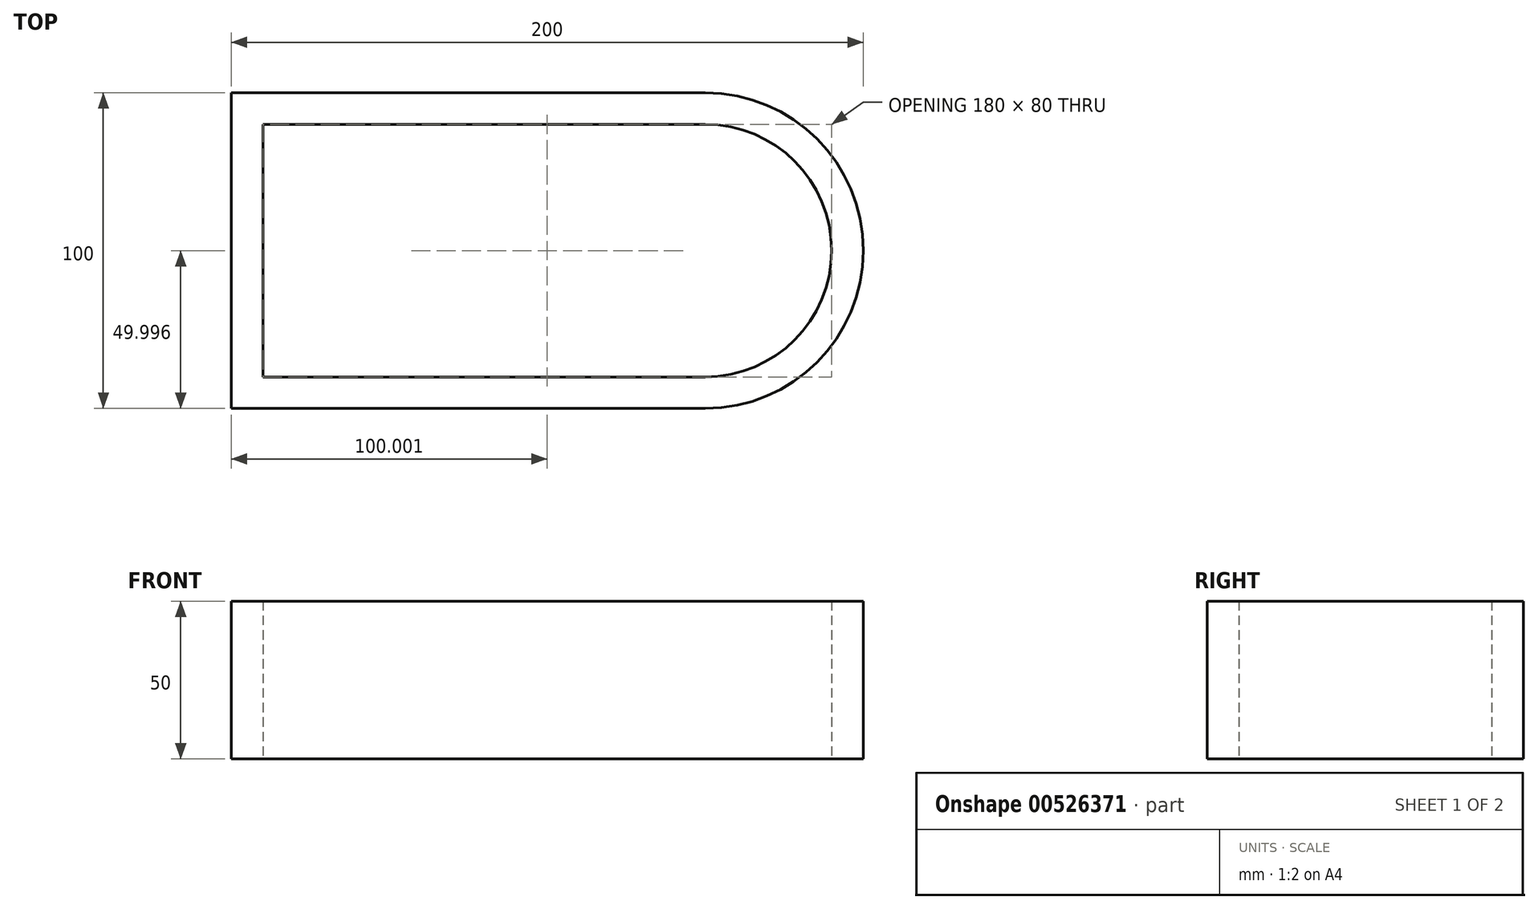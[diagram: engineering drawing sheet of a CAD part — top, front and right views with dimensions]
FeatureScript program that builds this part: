
annotation { "Feature Type Name" : "Feature", "Feature Type Description" : "" }
export const myFeature = defineFeature(function(context is Context, id is Id, definition is map)
    precondition{}
    {
        {
            var Q0;
            Q0=qCreatedBy(makeId("Top.planeOp"),FACE);
            var sketch = newSketch(context, id + "F0", { "sketchPlane" : qUnion([Q0])});
            skLineSegment(sketch, "E0.bottom", {"start": v(-110.52, 48.32) * mm, "end": v(39.48, 48.32) * mm});
            skLineSegment(sketch, "E0.top", {"start": v(-110.52, -51.68) * mm, "end": v(39.48, -51.68) * mm});
            skLineSegment(sketch, "E0.left", {"start": v(-110.52, 48.32) * mm, "end": v(-110.52, -51.68) * mm});
            skLineSegment(sketch, "E0.right", {"start": v(39.48, 48.32) * mm, "end": v(39.48, -51.68) * mm});
            skArc(sketch, "E1", {"start": v(39.48, -51.68) * mm, "mid": v(89.48, -1.68) * mm, "end": v(39.48, 48.32) * mm});
            skLineSegment(sketch, "E2.bottom", {"start": v(-100.52, 38.32) * mm, "end": v(39.48, 38.32) * mm});
            skLineSegment(sketch, "E2.top", {"start": v(-100.52, -41.68) * mm, "end": v(39.48, -41.68) * mm});
            skLineSegment(sketch, "E2.left", {"start": v(-100.52, 38.32) * mm, "end": v(-100.52, -41.68) * mm});
            skLineSegment(sketch, "E2.right", {"start": v(39.48, 38.32) * mm, "end": v(39.48, -41.68) * mm});
            skArc(sketch, "E3", {"start": v(39.48, -41.68) * mm, "mid": v(79.48, -1.68) * mm, "end": v(39.48, 38.32) * mm});
            skSolve(sketch);
        }
        {
            var Q0;
            Q0=makeQuery(id+"F0.imprint","IMPRINT",FACE,{"disambiguationData":[TD([[makeQuery(id+"F0.imprint","IMPRINT",EDGE,{"derivedFrom":sQuery(id+"F0.wireOp",EDGE,"E0.bottom")}),-1.0]])]});
            var Q1;
            Q1=makeQuery(id+"F0.imprint","IMPRINT",FACE,{"disambiguationData":[TD([[makeQuery(id+"F0.imprint","IMPRINT",EDGE,{"derivedFrom":sQuery(id+"F0.wireOp",EDGE,"E0.right")}),1.0]])]});
            extrude(context, id + "F1", {"entities" : qUnion([Q0, Q1]), "depth" : 50 * mm, "offsetDistance" : 25 * mm});
        }
    });
